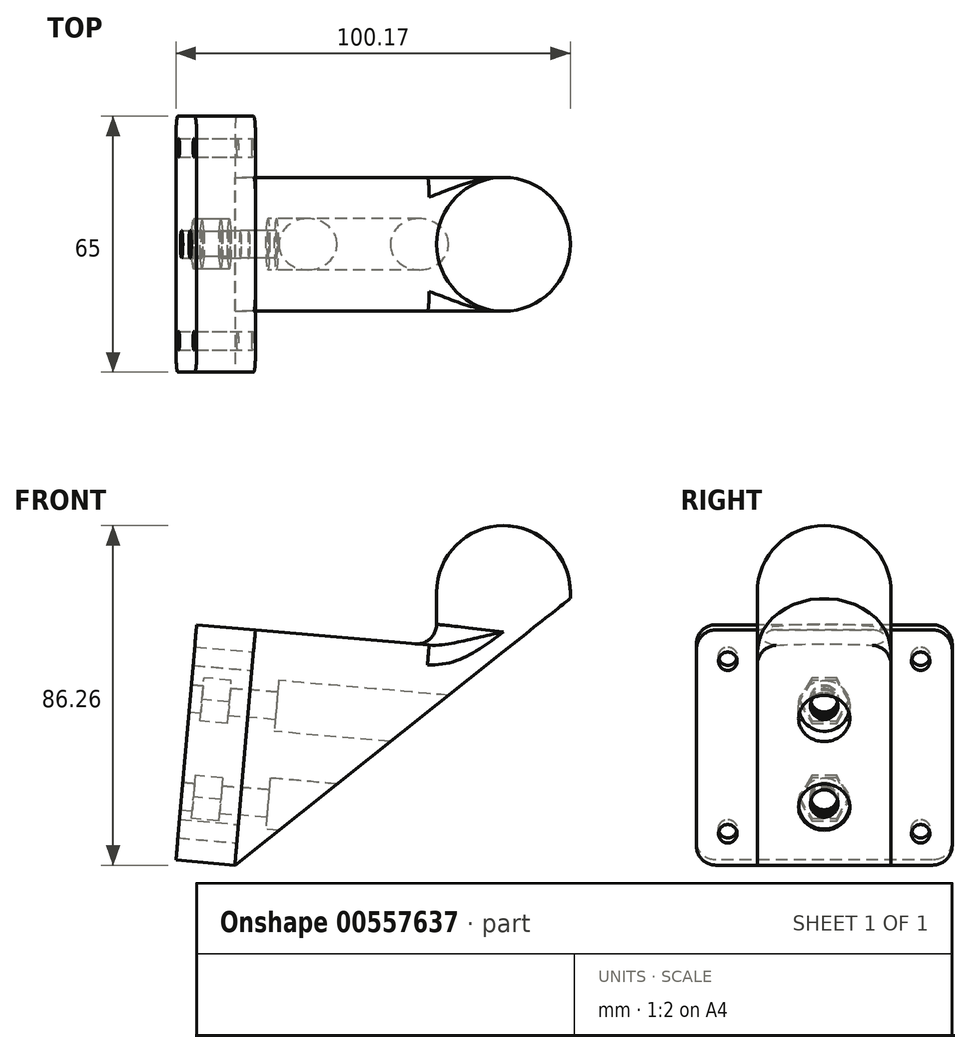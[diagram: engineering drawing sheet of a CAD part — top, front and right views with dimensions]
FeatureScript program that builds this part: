
annotation { "Feature Type Name" : "Feature", "Feature Type Description" : "" }
export const myFeature = defineFeature(function(context is Context, id is Id, definition is map)
    precondition{}
    {
        {
            var Q0;
            Q0=qCreatedBy(makeId("Top.planeOp"),FACE);
            var sketch = newSketch(context, id + "F0", { "sketchPlane" : qUnion([Q0])});
            skCircle(sketch, "E0", {"center": v(0, 0) * mm, "radius": 17 * mm});
            skSolve(sketch);
        }
        {
            var Q0;
            Q0 = qSketchRegion(id + "F0", true);
            extrude(context, id + "F1", {"entities" : qUnion([Q0]), "depth" : 15 * mm, "offsetDistance" : 25 * mm});
        }
        {
            var Q0;
            Q0=qCreatedBy(makeId("Front.planeOp"),FACE);
            var sketch = newSketch(context, id + "F2", { "sketchPlane" : qUnion([Q0])});
            skLineSegment(sketch, "E1.0", {"start": v(0, 15) * mm, "end": v(17, 15) * mm});
            skArc(sketch, "E2", {"start": v(17, 15) * mm, "mid": v(12.02, 27.02) * mm, "end": v(0, 32) * mm});
            skLineSegment(sketch, "E3", {"start": v(0, 32) * mm, "end": v(0, 15) * mm});
            skSolve(sketch);
        }
        {
            var Q0;
            Q0 = qSketchRegion(id + "F2", true);
            var Q1;
            Q1=sQuery(id+"F2.wireOp",EDGE,"E3");
            revolve(context, id + "F3", {"operationType" : NewBodyOperationType.ADD, "entities" : qUnion([Q0]), "axis" : qUnion([Q1]), "revolveType" : RevolveType.FULL});
        }
        {
            var Q0;
            Q0=qCreatedBy(makeId("Front.planeOp"),FACE);
            var sketch = newSketch(context, id + "F4", { "sketchPlane" : qUnion([Q0])});
            skLineSegment(sketch, "E4", {"start": v(-17, 0) * mm, "end": v(-17, 15) * mm});
            skLineSegment(sketch, "E5", {"start": v(17, 12.15) * mm, "end": v(17, 0) * mm});
            skLineSegment(sketch, "E6", {"start": v(0, 0) * mm, "end": v(-63, 5.51) * mm});
            skLineSegment(sketch, "E7", {"start": v(-63, 5.51) * mm, "end": v(-68.23, -54.26) * mm});
            skLineSegment(sketch, "E8", {"start": v(-68.23, -54.26) * mm, "end": v(0, 0) * mm});
            skSolve(sketch);
        }
        {
            var Q0;
            {var subQ2=sQuery(id+"F4.wireOp",EDGE,"E7");Q0=makeQuery(id+"F4.imprint","IMPRINT",FACE,{"disambiguationData":[TD([[makeQuery(id+"F4.imprint","IMPRINT",EDGE,{"derivedFrom":subQ2}),1.0]])]});}
            var Q1;
            Q1=makeQuery(id+"F1.opExtrude","CAP_FACE",FACE,{"disambiguationData":[OSD([sQuery(id+"F0.wireOp",EDGE,"E0")])],"isStart":true});
            var Q2;
            Q2=makeQuery(id+"F1.opExtrude","SWEPT_BODY",BODY,{"disambiguationData":[OSD([sQuery(id+"F0.wireOp",EDGE,"E0")])]});
            extrude(context, id + "F5", {"entities" : qUnion([Q0]), "operationType" : NewBodyOperationType.ADD, "endBound" : BoundingType.SYMMETRIC, "depth" : 34 * mm, "endBoundEntityFace" : qUnion([Q1]), "endBoundEntityBody" : qUnion([Q2]), "offsetDistance" : 25 * mm});
        }
        {
            var Q0;
            Q0=makeQuery(id+"F5.opExtrude","SWEPT_FACE",FACE,{"disambiguationData":[OSD([sQuery(id+"F4.wireOp",EDGE,"E7")])]});
            var sketch = newSketch(context, id + "F6", { "sketchPlane" : qUnion([Q0])});
            skCircle(sketch, "E9", {"center": v(0, -18.78) * mm, "radius": 3.5 * mm});
            skCircle(sketch, "E10", {"center": v(0, -43.68) * mm, "radius": 3.5 * mm});
            skCircle(sketch, "E11", {"center": v(0, -43.68) * mm, "radius": 6.5 * mm});
            skCircle(sketch, "E12", {"center": v(0, -18.78) * mm, "radius": 6.5 * mm});
            skSolve(sketch);
        }
        {
            var Q0;
            Q0=makeQuery(id+"F6.imprint","IMPRINT",FACE,{"disambiguationData":[TD([[makeQuery(id+"F6.imprint","IMPRINT",EDGE,{"derivedFrom":sQuery(id+"F6.wireOp",EDGE,"E9")}),1.0]])]});
            var Q1;
            Q1=makeQuery(id+"F6.imprint","IMPRINT",FACE,{"disambiguationData":[TD([[makeQuery(id+"F6.imprint","IMPRINT",EDGE,{"derivedFrom":sQuery(id+"F6.wireOp",EDGE,"E10")}),1.0]])]});
            extrude(context, id + "F7", {"entities" : qUnion([Q0, Q1]), "operationType" : NewBodyOperationType.REMOVE, "endBound" : BoundingType.THROUGH_ALL, "oppositeDirection" : true, "depth" : 25 * mm, "offsetDistance" : 25 * mm});
        }
        {
            var Q0;
            Q0=makeQuery(id+"F6.imprint","IMPRINT",FACE,{"disambiguationData":[TD([[makeQuery(id+"F6.imprint","IMPRINT",EDGE,{"derivedFrom":sQuery(id+"F6.wireOp",EDGE,"E10")}),-1.0]])]});
            var Q1;
            Q1=makeQuery(id+"F6.imprint","IMPRINT",FACE,{"disambiguationData":[TD([[makeQuery(id+"F6.imprint","IMPRINT",EDGE,{"derivedFrom":sQuery(id+"F6.wireOp",EDGE,"E9")}),-1.0]])]});
            var Q2;
            Q2=sQuery(id+"F6.wireOp",EDGE,"E12");
            var Q3;
            Q3=sQuery(id+"F6.wireOp",EDGE,"E11");
            extrude(context, id + "F8", {"entities" : qUnion([Q0, Q1]), "operationType" : NewBodyOperationType.REMOVE, "surfaceEntities" : qUnion([Q2, Q3]), "oppositeDirection" : true, "depth" : 100 * mm, "offsetDistance" : 25 * mm, "hasSecondDirection" : true, "secondDirectionOppositeDirection" : true, "secondDirectionDepth" : 7 * mm});
        }
        {
            var Q0;
            Q0=makeQuery(id+"F6.imprint","IMPRINT",FACE,{"disambiguationData":[TD([[makeQuery(id+"F6.imprint","IMPRINT",EDGE,{"derivedFrom":sQuery(id+"F6.wireOp",EDGE,"E11")}),-1.0]])]});
            cPlane(context, id + "F9", {"entities" : qUnion([Q0]), "cplaneType" : CPlaneType.OFFSET, "offset" : 0 * mm, "width" : 150 * mm, "height" : 150 * mm});
        }
        {
            var Q0;
            Q0=qCreatedBy(id+"F9.planeOp",FACE);
            var sketch = newSketch(context, id + "F10", { "sketchPlane" : qUnion([Q0])});
            skLineSegment(sketch, "E13.bottom", {"start": v(-32.5, -60) * mm, "end": v(32.5, -60) * mm});
            skLineSegment(sketch, "E13.top", {"start": v(-32.5, 0) * mm, "end": v(32.5, 0) * mm});
            skLineSegment(sketch, "E13.left", {"start": v(-32.5, -60) * mm, "end": v(-32.5, 0) * mm});
            skLineSegment(sketch, "E13.right", {"start": v(32.5, -60) * mm, "end": v(32.5, 0) * mm});
            skSolve(sketch);
        }
        {
            var Q0;
            Q0=makeQuery(id+"F10.imprint","IMPRINT",FACE,{"disambiguationData":[TD([[makeQuery(id+"F10.imprint","IMPRINT",EDGE,{"derivedFrom":sQuery(id+"F10.wireOp",EDGE,"E13.bottom")}),1.0]])]});
            extrude(context, id + "F11", {"entities" : qUnion([Q0]), "depth" : 15 * mm, "offsetDistance" : 25 * mm});
        }
        {
            var Q0;
            Q0=makeQuery(id+"F11.opExtrude","CAP_FACE",FACE,{"disambiguationData":[OSD([sQuery(id+"F10.wireOp",EDGE,"E13.bottom"),sQuery(id+"F10.wireOp",EDGE,"E13.top"),sQuery(id+"F10.wireOp",EDGE,"E13.left"),sQuery(id+"F10.wireOp",EDGE,"E13.right")])],"isStart":true});
            var sketch = newSketch(context, id + "F12", { "sketchPlane" : qUnion([Q0])});
            skLineSegment(sketch, "E14.0", {"start": v(24.5, -52) * mm, "end": v(-24.5, -52) * mm, "construction": true});
            skLineSegment(sketch, "E14.1", {"start": v(24.5, -52) * mm, "end": v(24.5, -8) * mm, "construction": true});
            skLineSegment(sketch, "E14.2", {"start": v(24.5, -8) * mm, "end": v(-24.5, -8) * mm, "construction": true});
            skLineSegment(sketch, "E14.3", {"start": v(-24.5, -52) * mm, "end": v(-24.5, -8) * mm, "construction": true});
            skCircle(sketch, "E15", {"center": v(-24.5, -52) * mm, "radius": 2.35 * mm});
            skCircle(sketch, "E16", {"center": v(-24.5, -8) * mm, "radius": 2.35 * mm});
            skCircle(sketch, "E17", {"center": v(24.5, -8) * mm, "radius": 2.35 * mm});
            skCircle(sketch, "E18", {"center": v(24.5, -52) * mm, "radius": 2.35 * mm});
            skSolve(sketch);
        }
        {
            var Q0;
            Q0 = qSketchRegion(id + "F12", true);
            var Q1;
            Q1=makeQuery(id+"F11.opExtrude","CAP_FACE",FACE,{"disambiguationData":[OSD([sQuery(id+"F10.wireOp",EDGE,"E13.bottom"),sQuery(id+"F10.wireOp",EDGE,"E13.top"),sQuery(id+"F10.wireOp",EDGE,"E13.left"),sQuery(id+"F10.wireOp",EDGE,"E13.right")])],"isStart":false});
            extrude(context, id + "F13", {"entities" : qUnion([Q0]), "operationType" : NewBodyOperationType.REMOVE, "endBound" : BoundingType.UP_TO_SURFACE, "oppositeDirection" : true, "depth" : 25 * mm, "endBoundEntityFace" : qUnion([Q1]), "offsetDistance" : 25 * mm});
        }
        {
            var Q0;
            Q0=makeQuery(id+"F11.opExtrude","CAP_FACE",FACE,{"disambiguationData":[OSD([sQuery(id+"F10.wireOp",EDGE,"E13.bottom"),sQuery(id+"F10.wireOp",EDGE,"E13.top"),sQuery(id+"F10.wireOp",EDGE,"E13.left"),sQuery(id+"F10.wireOp",EDGE,"E13.right")])],"isStart":false});
            var sketch = newSketch(context, id + "F14", { "sketchPlane" : qUnion([Q0])});
            skPoint(sketch, "E19.0", {"position": v(0, -43.68) * mm});
            skPoint(sketch, "E20.0", {"position": v(0, -18.78) * mm});
            skCircle(sketch, "E21.cCircle", {"center": v(0, -43.68) * mm, "radius": 5.5 * mm, "construction": true});
            skLineSegment(sketch, "E21.0", {"start": v(-3.18, -49.18) * mm, "end": v(-6.35, -43.68) * mm});
            skLineSegment(sketch, "E21.1", {"start": v(-6.35, -43.68) * mm, "end": v(-3.18, -38.18) * mm});
            skLineSegment(sketch, "E21.2", {"start": v(-3.18, -38.18) * mm, "end": v(3.18, -38.18) * mm});
            skLineSegment(sketch, "E21.3", {"start": v(3.18, -38.18) * mm, "end": v(6.35, -43.68) * mm});
            skLineSegment(sketch, "E21.4", {"start": v(6.35, -43.68) * mm, "end": v(3.18, -49.18) * mm});
            skLineSegment(sketch, "E21.5", {"start": v(3.18, -49.18) * mm, "end": v(-3.18, -49.18) * mm});
            skPoint(sketch, "E21.0.midPoint", {"position": v(-4.76, -46.43) * mm});
            skCircle(sketch, "E22.cCircle", {"center": v(0, -18.78) * mm, "radius": 5.5 * mm, "construction": true});
            skLineSegment(sketch, "E22.0", {"start": v(-6.35, -18.78) * mm, "end": v(-3.18, -13.28) * mm});
            skLineSegment(sketch, "E22.1", {"start": v(-3.18, -13.28) * mm, "end": v(3.18, -13.28) * mm});
            skLineSegment(sketch, "E22.2", {"start": v(3.18, -13.28) * mm, "end": v(6.35, -18.78) * mm});
            skLineSegment(sketch, "E22.3", {"start": v(6.35, -18.78) * mm, "end": v(3.18, -24.28) * mm});
            skLineSegment(sketch, "E22.4", {"start": v(3.18, -24.28) * mm, "end": v(-3.18, -24.28) * mm});
            skLineSegment(sketch, "E22.5", {"start": v(-3.18, -24.28) * mm, "end": v(-6.35, -18.78) * mm});
            skPoint(sketch, "E22.0.midPoint", {"position": v(-4.76, -16.03) * mm});
            skSolve(sketch);
        }
        {
            var Q0;
            Q0=makeQuery(id+"F14.imprint","IMPRINT",FACE,{"disambiguationData":[TD([[makeQuery(id+"F14.imprint","IMPRINT",EDGE,{"derivedFrom":sQuery(id+"F14.wireOp",EDGE,"E21.0")}),-1.0]])]});
            var Q1;
            Q1=makeQuery(id+"F14.imprint","IMPRINT",FACE,{"disambiguationData":[TD([[makeQuery(id+"F14.imprint","IMPRINT",EDGE,{"derivedFrom":sQuery(id+"F14.wireOp",EDGE,"E22.0")}),-1.0]])]});
            extrude(context, id + "F15", {"entities" : qUnion([Q0, Q1]), "operationType" : NewBodyOperationType.REMOVE, "oppositeDirection" : true, "depth" : 10 * mm, "offsetDistance" : 25 * mm, "hasSecondDirection" : true, "secondDirectionOppositeDirection" : true, "secondDirectionDepth" : 3 * mm});
        }
        {
            var Q0;
            Q0=makeQuery(id+"F6.imprint","IMPRINT",FACE,{"disambiguationData":[TD([[makeQuery(id+"F6.imprint","IMPRINT",EDGE,{"derivedFrom":sQuery(id+"F6.wireOp",EDGE,"E10")}),1.0]])]});
            var Q1;
            Q1=makeQuery(id+"F6.imprint","IMPRINT",FACE,{"disambiguationData":[TD([[makeQuery(id+"F6.imprint","IMPRINT",EDGE,{"derivedFrom":sQuery(id+"F6.wireOp",EDGE,"E9")}),1.0]])]});
            var Q2;
            Q2=makeQuery(id+"F11.opExtrude","CAP_FACE",FACE,{"disambiguationData":[OSD([sQuery(id+"F10.wireOp",EDGE,"E13.bottom"),sQuery(id+"F10.wireOp",EDGE,"E13.top"),sQuery(id+"F10.wireOp",EDGE,"E13.left"),sQuery(id+"F10.wireOp",EDGE,"E13.right")])],"isStart":false});
            extrude(context, id + "F16", {"entities" : qUnion([Q0, Q1]), "operationType" : NewBodyOperationType.REMOVE, "endBound" : BoundingType.UP_TO_SURFACE, "depth" : 25 * mm, "endBoundEntityFace" : qUnion([Q2]), "offsetDistance" : 25 * mm});
        }
        {
            var Q0;
            Q0=makeQuery(id+"F5.opExtrude","CAP_FACE",FACE,{"disambiguationData":[OSD([sQuery(id+"F4.wireOp",EDGE,"E6"),sQuery(id+"F4.wireOp",EDGE,"E7"),sQuery(id+"F4.wireOp",EDGE,"E8")])],"isStart":false});
            var sketch = newSketch(context, id + "F17", { "sketchPlane" : qUnion([Q0])});
            skLineSegment(sketch, "E23", {"start": v(0, 0) * mm, "end": v(20.03, 15.93) * mm});
            skLineSegment(sketch, "E24", {"start": v(20.03, 15.93) * mm, "end": v(20.03, 0) * mm});
            skLineSegment(sketch, "E25", {"start": v(20.03, 0) * mm, "end": v(0, 0) * mm});
            skSolve(sketch);
        }
        {
            var Q0;
            Q0 = qSketchRegion(id + "F17", true);
            extrude(context, id + "F18", {"entities" : qUnion([Q0]), "operationType" : NewBodyOperationType.REMOVE, "oppositeDirection" : true, "depth" : 35 * mm, "offsetDistance" : 25 * mm});
        }
        {
            var Q0;
            Q0=makeQuery(id+"F5.boolean.opBoolean","INTERSECT",EDGE,{"derivedFrom":[makeQuery(id+"F1.opExtrude","SWEPT_FACE",FACE,{"disambiguationData":[OSD([sQuery(id+"F0.wireOp",EDGE,"E0")])]}),makeQuery(id+"F5.opExtrude","SWEPT_FACE",FACE,{"disambiguationData":[OSD([sQuery(id+"F4.wireOp",EDGE,"E6")])]})]});
            fillet(context, id + "F19", {"entities" : qUnion([Q0]), "radius" : 5 * mm, "tangentPropagation" : true, "allowEdgeOverflow" : false});
        }
        {
            var Q0;
            Q0=makeQuery(id+"F5.opExtrude","CAP_EDGE",EDGE,{"disambiguationData":[OSD([sQuery(id+"F4.wireOp",EDGE,"E6")])],"isStart":false});
            var Q1;
            Q1=makeQuery(id+"F5.opExtrude","CAP_EDGE",EDGE,{"disambiguationData":[OSD([sQuery(id+"F4.wireOp",EDGE,"E6")])],"isStart":true});
            fillet(context, id + "F20", {"entities" : qUnion([Q0, Q1]), "radius" : 5 * mm, "tangentPropagation" : true, "allowEdgeOverflow" : false});
        }
        {
            var Q0;
            Q0=makeQuery(id+"F11.opExtrude","SWEPT_EDGE",EDGE,{"disambiguationData":[OSD([sQuery(id+"F10.wireOp",EDGE,"E13.top"),sQuery(id+"F10.wireOp",EDGE,"E13.right")])]});
            var Q1;
            Q1=makeQuery(id+"F11.opExtrude","SWEPT_EDGE",EDGE,{"disambiguationData":[OSD([sQuery(id+"F10.wireOp",EDGE,"E13.bottom"),sQuery(id+"F10.wireOp",EDGE,"E13.right")])]});
            var Q2;
            Q2=makeQuery(id+"F11.opExtrude","SWEPT_EDGE",EDGE,{"disambiguationData":[OSD([sQuery(id+"F10.wireOp",EDGE,"E13.top"),sQuery(id+"F10.wireOp",EDGE,"E13.left")])]});
            var Q3;
            Q3=makeQuery(id+"F11.opExtrude","SWEPT_EDGE",EDGE,{"disambiguationData":[OSD([sQuery(id+"F10.wireOp",EDGE,"E13.bottom"),sQuery(id+"F10.wireOp",EDGE,"E13.left")])]});
            fillet(context, id + "F21", {"entities" : qUnion([Q0, Q1, Q2, Q3]), "radius" : 5 * mm, "tangentPropagation" : true, "allowEdgeOverflow" : false});
        }
    });
